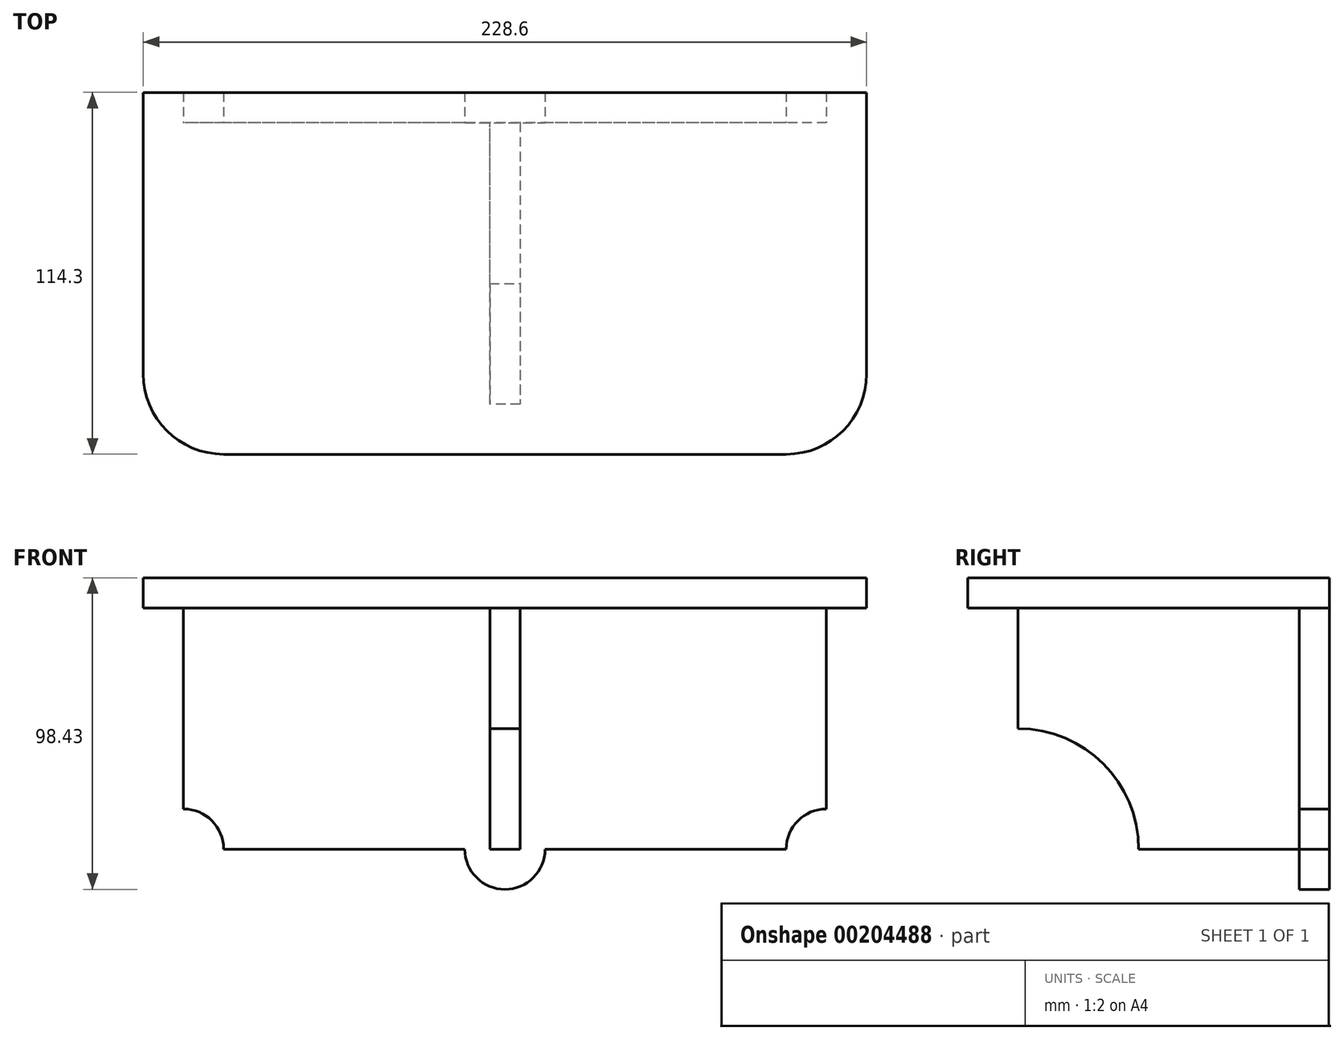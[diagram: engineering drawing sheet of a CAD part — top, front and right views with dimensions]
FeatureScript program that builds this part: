
annotation { "Feature Type Name" : "Feature", "Feature Type Description" : "" }
export const myFeature = defineFeature(function(context is Context, id is Id, definition is map)
    precondition{}
    {
        {
            var Q0;
            Q0=qCreatedBy(makeId("Top.planeOp"),FACE);
            var sketch = newSketch(context, id + "F0", { "sketchPlane" : qUnion([Q0])});
            skLineSegment(sketch, "E0.bottom", {"start": v(-110.67, 55.07) * mm, "end": v(117.93, 55.07) * mm});
            skLineSegment(sketch, "E0.top", {"start": v(-110.67, -59.23) * mm, "end": v(117.93, -59.23) * mm});
            skLineSegment(sketch, "E0.left", {"start": v(-110.67, 55.07) * mm, "end": v(-110.67, -59.23) * mm});
            skLineSegment(sketch, "E0.right", {"start": v(117.93, 55.07) * mm, "end": v(117.93, -59.23) * mm});
            skSolve(sketch);
        }
        {
            var Q0;
            Q0=makeQuery(id+"F0.imprint","IMPRINT",FACE,{"disambiguationData":[TD([[makeQuery(id+"F0.imprint","IMPRINT",EDGE,{"derivedFrom":sQuery(id+"F0.wireOp",EDGE,"E0.bottom")}),-1.0]])]});
            extrude(context, id + "F1", {"entities" : qUnion([Q0]), "depth" : 9.52 * mm});
        }
        {
            var Q0;
            Q0=makeQuery(id+"F1.opExtrude","SWEPT_EDGE",EDGE,{"disambiguationData":[OSD([sQuery(id+"F0.wireOp",EDGE,"E0.top"),sQuery(id+"F0.wireOp",EDGE,"E0.right")])]});
            var Q1;
            Q1=makeQuery(id+"F1.opExtrude","SWEPT_EDGE",EDGE,{"disambiguationData":[OSD([sQuery(id+"F0.wireOp",EDGE,"E0.top"),sQuery(id+"F0.wireOp",EDGE,"E0.left")])]});
            fillet(context, id + "F2", {"entities" : qUnion([Q0, Q1]), "radius" : 25.4 * mm, "tangentPropagation" : true, "allowEdgeOverflow" : false});
        }
        {
            var Q0;
            Q0=makeQuery(id+"F1.opExtrude","CAP_FACE",FACE,{"disambiguationData":[OSD([sQuery(id+"F0.wireOp",EDGE,"E0.bottom"),sQuery(id+"F0.wireOp",EDGE,"E0.top"),sQuery(id+"F0.wireOp",EDGE,"E0.left"),sQuery(id+"F0.wireOp",EDGE,"E0.right")])],"isStart":true});
            var sketch = newSketch(context, id + "F3", { "sketchPlane" : qUnion([Q0])});
            skLineSegment(sketch, "E1", {"start": v(117.93, -55.07) * mm, "end": v(105.23, -55.07) * mm});
            skLineSegment(sketch, "E2", {"start": v(-110.67, -55.07) * mm, "end": v(-97.97, -55.07) * mm});
            skLineSegment(sketch, "E3", {"start": v(-97.97, -55.07) * mm, "end": v(-97.97, -45.54) * mm});
            skLineSegment(sketch, "E4", {"start": v(105.23, -45.54) * mm, "end": v(-97.97, -45.54) * mm});
            skLineSegment(sketch, "E5", {"start": v(105.23, -55.07) * mm, "end": v(105.23, -45.54) * mm});
            skSolve(sketch);
        }
        {
            var Q0;
            Q0 = qSketchRegion(id + "F3", true);
            var Q1;
            {var subQ0=sQuery(id+"F3.wireOp",EDGE,"E3");Q1=makeQuery(id+"F3.imprint","IMPRINT",FACE,{"disambiguationData":[TD([[makeQuery(id+"F3.imprint","IMPRINT",EDGE,{"derivedFrom":subQ0}),-1.0]])]});}
            extrude(context, id + "F4", {"entities" : qUnion([Q0, Q1]), "operationType" : NewBodyOperationType.ADD, "depth" : 76.2 * mm});
        }
        {
            var Q0;
            Q0=makeQuery(id+"F4.opExtrude","SWEPT_FACE",FACE,{"disambiguationData":[OSD([sQuery(id+"F3.wireOp",EDGE,"E4")])]});
            var sketch = newSketch(context, id + "F5", { "sketchPlane" : qUnion([Q0])});
            skCircle(sketch, "E6", {"center": v(-97.97, -76.2) * mm, "radius": 12.7 * mm});
            skCircle(sketch, "E7", {"center": v(105.23, -76.2) * mm, "radius": 12.7 * mm});
            skCircle(sketch, "E8", {"center": v(3.63, -76.2) * mm, "radius": 12.7 * mm});
            skSolve(sketch);
        }
        {
            var Q0;
            {var subQ0=sQuery(id+"F5.wireOp",EDGE,"E8");var subQ1=makeQuery(id+"F4.opExtrude","CAP_EDGE",EDGE,{"disambiguationData":[OSD([sQuery(id+"F3.wireOp",EDGE,"E4")])],"isStart":false});var subQ2=makeQuery(id+"F5.imprint","INTERSECT",VERTEX,{"disambiguationData":[OD(0.0)],"derivedFrom":[subQ1,subQ0]});Q0=makeQuery(id+"F5.imprint","IMPRINT",FACE,{"disambiguationData":[TD([[makeQuery(id+"F5.imprint","IMPRINT",EDGE,{"disambiguationData":[TD([[subQ2,-1.0]])],"derivedFrom":subQ0}),1.0]])]});}
            var Q1;
            {var subQ0=sQuery(id+"F5.wireOp",EDGE,"E6");var subQ1=sQuery(id+"F3.wireOp",EDGE,"E4");var subQ4=makeQuery(id+"F4.opExtrude","CAP_EDGE",EDGE,{"disambiguationData":[OSD([subQ1])],"isStart":false});var subQ5=makeQuery(id+"F5.imprint","INTERSECT",VERTEX,{"derivedFrom":[subQ4,subQ0]});Q1=makeQuery(id+"F5.imprint","IMPRINT",FACE,{"disambiguationData":[TD([[makeQuery(id+"F5.imprint","IMPRINT",EDGE,{"disambiguationData":[TD([[subQ5,-1.0]])],"derivedFrom":subQ0}),1.0]])]});}
            extrude(context, id + "F6", {"entities" : qUnion([Q0, Q1]), "operationType" : NewBodyOperationType.REMOVE, "oppositeDirection" : true, "depth" : 9.52 * mm});
        }
        {
            var Q0;
            {var subQ0=sQuery(id+"F5.wireOp",EDGE,"E8");var subQ1=makeQuery(id+"F4.opExtrude","CAP_EDGE",EDGE,{"disambiguationData":[OSD([sQuery(id+"F3.wireOp",EDGE,"E4")])],"isStart":false});var subQ2=makeQuery(id+"F5.imprint","INTERSECT",VERTEX,{"disambiguationData":[OD(0.0)],"derivedFrom":[subQ1,subQ0]});Q0=makeQuery(id+"F5.imprint","IMPRINT",FACE,{"disambiguationData":[TD([[makeQuery(id+"F5.imprint","IMPRINT",EDGE,{"disambiguationData":[TD([[subQ2,-1.0]])],"derivedFrom":subQ0}),1.0]])]});}
            var Q1;
            {var subQ0=sQuery(id+"F5.wireOp",EDGE,"E7");var subQ1=sQuery(id+"F3.wireOp",EDGE,"E4");var subQ4=makeQuery(id+"F4.opExtrude","CAP_EDGE",EDGE,{"disambiguationData":[OSD([subQ1])],"isStart":false});var subQ5=makeQuery(id+"F5.imprint","INTERSECT",VERTEX,{"derivedFrom":[subQ4,subQ0]});Q1=makeQuery(id+"F5.imprint","IMPRINT",FACE,{"disambiguationData":[TD([[makeQuery(id+"F5.imprint","IMPRINT",EDGE,{"disambiguationData":[TD([[subQ5,1.0]])],"derivedFrom":subQ0}),1.0]])]});}
            extrude(context, id + "F7", {"entities" : qUnion([Q0, Q1]), "operationType" : NewBodyOperationType.REMOVE, "oppositeDirection" : true, "depth" : 9.52 * mm});
        }
        {
            var Q0;
            {var subQ0=sQuery(id+"F5.wireOp",EDGE,"E8");var subQ1=makeQuery(id+"F4.opExtrude","CAP_EDGE",EDGE,{"disambiguationData":[OSD([sQuery(id+"F3.wireOp",EDGE,"E4")])],"isStart":false});var subQ2=makeQuery(id+"F5.imprint","INTERSECT",VERTEX,{"disambiguationData":[OD(0.0)],"derivedFrom":[subQ1,subQ0]});Q0=makeQuery(id+"F5.imprint","IMPRINT",FACE,{"disambiguationData":[TD([[makeQuery(id+"F5.imprint","IMPRINT",EDGE,{"disambiguationData":[TD([[subQ2,-1.0]])],"derivedFrom":subQ0}),1.0]])]});}
            extrude(context, id + "F8", {"entities" : qUnion([Q0]), "oppositeDirection" : true, "depth" : 9.52 * mm});
        }
        {
            var Q0;
            Q0=makeQuery(id+"F1.opExtrude","CAP_FACE",FACE,{"disambiguationData":[OSD([sQuery(id+"F0.wireOp",EDGE,"E0.bottom"),sQuery(id+"F0.wireOp",EDGE,"E0.top"),sQuery(id+"F0.wireOp",EDGE,"E0.left"),sQuery(id+"F0.wireOp",EDGE,"E0.right")])],"isStart":true});
            var sketch = newSketch(context, id + "F9", { "sketchPlane" : qUnion([Q0])});
            skLineSegment(sketch, "E9", {"start": v(3.63, -45.54) * mm, "end": v(-1.13, -45.54) * mm});
            skLineSegment(sketch, "E10", {"start": v(-1.13, -45.54) * mm, "end": v(3.63, -45.54) * mm});
            skLineSegment(sketch, "E11", {"start": v(3.63, -45.54) * mm, "end": v(8.4, -45.54) * mm});
            skLineSegment(sketch, "E12", {"start": v(8.4, -45.54) * mm, "end": v(8.4, 43.36) * mm});
            skLineSegment(sketch, "E13", {"start": v(-1.13, 43.36) * mm, "end": v(-1.13, -45.54) * mm});
            skLineSegment(sketch, "E14", {"start": v(8.4, 43.36) * mm, "end": v(-1.13, 43.36) * mm});
            skSolve(sketch);
        }
        {
            var Q0;
            Q0 = qSketchRegion(id + "F9", true);
            extrude(context, id + "F10", {"entities" : qUnion([Q0]), "operationType" : NewBodyOperationType.ADD, "depth" : 76.2 * mm});
        }
        {
            var Q0;
            Q0=makeQuery(id+"F10.opExtrude","SWEPT_FACE",FACE,{"disambiguationData":[OSD([sQuery(id+"F9.wireOp",EDGE,"E12")])]});
            var sketch = newSketch(context, id + "F11", { "sketchPlane" : qUnion([Q0])});
            skCircle(sketch, "E15", {"center": v(-43.36, -76.2) * mm, "radius": 38.1 * mm});
            skSolve(sketch);
        }
        {
            var Q0;
            {var subQ0=sQuery(id+"F11.wireOp",EDGE,"E15");var subQ1=sQuery(id+"F9.wireOp",EDGE,"E12");var subQ4=makeQuery(id+"F10.opExtrude","CAP_EDGE",EDGE,{"disambiguationData":[OSD([subQ1])],"isStart":false});var subQ5=makeQuery(id+"F11.imprint","INTERSECT",VERTEX,{"derivedFrom":[subQ4,subQ0]});Q0=makeQuery(id+"F11.imprint","IMPRINT",FACE,{"disambiguationData":[TD([[makeQuery(id+"F11.imprint","IMPRINT",EDGE,{"disambiguationData":[TD([[subQ5,-1.0]])],"derivedFrom":subQ0}),1.0]])]});}
            extrude(context, id + "F12", {"entities" : qUnion([Q0]), "operationType" : NewBodyOperationType.REMOVE, "oppositeDirection" : true, "depth" : 25.4 * mm});
        }
    });
